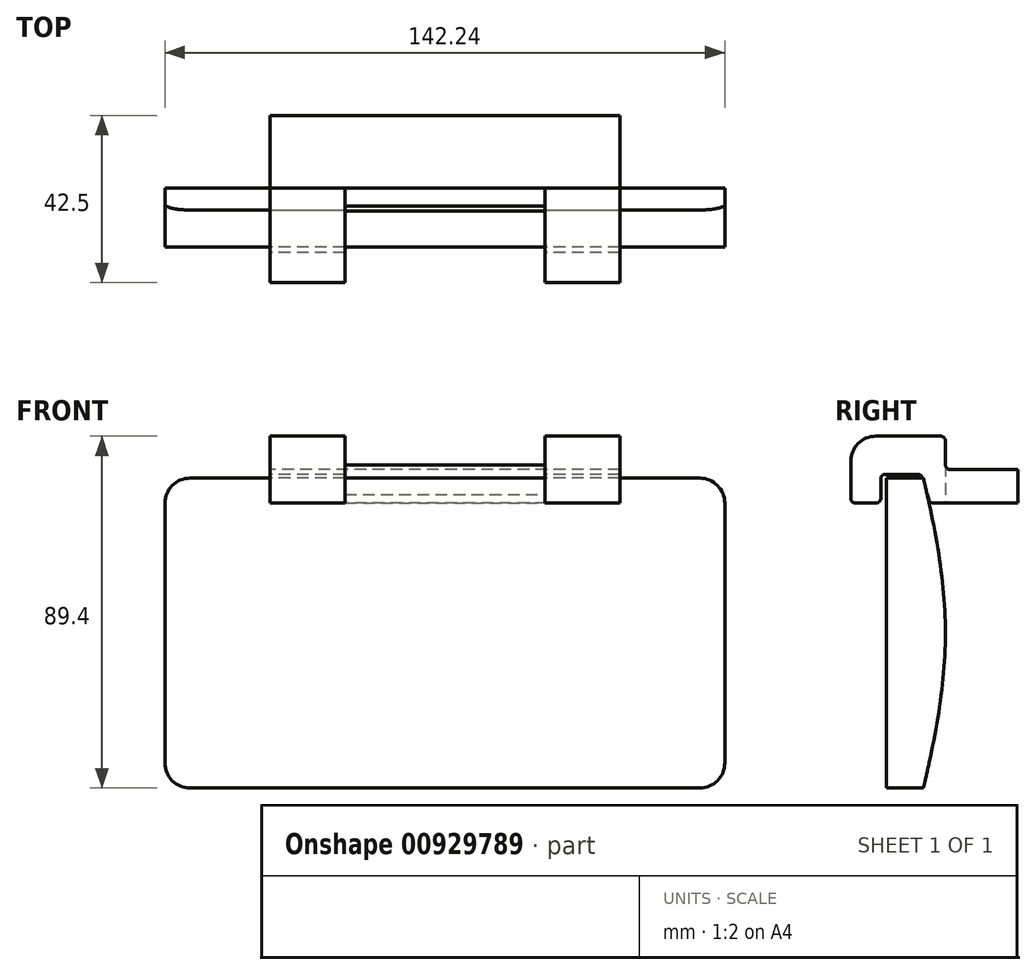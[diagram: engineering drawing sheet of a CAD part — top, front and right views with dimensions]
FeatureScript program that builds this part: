
annotation { "Feature Type Name" : "Feature", "Feature Type Description" : "" }
export const myFeature = defineFeature(function(context is Context, id is Id, definition is map)
    precondition{}
    {
        {
            var Q0;
            Q0=qCreatedBy(makeId("Front.planeOp"),FACE);
            var sketch = newSketch(context, id + "F0", { "sketchPlane" : qUnion([Q0])});
            skLineSegment(sketch, "E0.bottom", {"start": v(64.77, -39.37) * mm, "end": v(-64.77, -39.37) * mm});
            skLineSegment(sketch, "E0.top", {"start": v(64.77, 39.37) * mm, "end": v(-64.77, 39.37) * mm});
            skLineSegment(sketch, "E0.left", {"start": v(71.12, -33.02) * mm, "end": v(71.12, 33.02) * mm});
            skLineSegment(sketch, "E0.right", {"start": v(-71.12, -33.02) * mm, "end": v(-71.12, 33.02) * mm});
            skPoint(sketch, "E0.middle", {"position": v(0, 0) * mm});
            skLineSegment(sketch, "E1.0", {"start": v(71.12, 34.16) * mm, "end": v(-71.12, 34.16) * mm, "construction": true});
            skLineSegment(sketch, "E2.0", {"start": v(-65.91, -38.86) * mm, "end": v(-65.91, 39.37) * mm, "construction": true});
            skLineSegment(sketch, "E3.0", {"start": v(71.12, -34.16) * mm, "end": v(-71.12, -34.16) * mm, "construction": true});
            skLineSegment(sketch, "E4.0", {"start": v(65.91, -38.86) * mm, "end": v(65.91, 39.37) * mm, "construction": true});
            skPoint(sketch, "E5.visualSharp", {"position": v(71.12, 39.37) * mm});
            skArc(sketch, "E5.filletArc", {"start": v(71.12, 33.02) * mm, "mid": v(69.26, 37.51) * mm, "end": v(64.77, 39.37) * mm});
            skPoint(sketch, "E6.visualSharp", {"position": v(71.12, -39.37) * mm});
            skArc(sketch, "E6.filletArc", {"start": v(64.77, -39.37) * mm, "mid": v(69.26, -37.51) * mm, "end": v(71.12, -33.02) * mm});
            skPoint(sketch, "E7.visualSharp", {"position": v(-71.12, -39.37) * mm});
            skArc(sketch, "E7.filletArc", {"start": v(-71.12, -33.02) * mm, "mid": v(-69.26, -37.51) * mm, "end": v(-64.77, -39.37) * mm});
            skPoint(sketch, "E8.visualSharp", {"position": v(-71.12, 39.37) * mm});
            skArc(sketch, "E8.filletArc", {"start": v(-64.77, 39.37) * mm, "mid": v(-69.26, 37.51) * mm, "end": v(-71.12, 33.02) * mm});
            skSolve(sketch);
        }
        {
            var Q0;
            Q0=qSketchRegion(id+"F0",true);
            extrude(context, id + "F1", {"entities" : qUnion([Q0]), "depth" : 15 * mm});
        }
        {
            var Q0;
            Q0=makeQuery(id+"F1.opExtrude","SWEPT_FACE",FACE,{"disambiguationData":[OSD([sQuery(id+"F0.wireOp",EDGE,"E0.left")])]});
            var sketch = newSketch(context, id + "F2", { "sketchPlane" : qUnion([Q0])});
            skLineSegment(sketch, "E9", {"start": v(-14.99, 39.37) * mm, "end": v(-5.59, 39.37) * mm});
            skLineSegment(sketch, "E10", {"start": v(-14.99, 39.37) * mm, "end": v(-14.99, -39.37) * mm});
            skLineSegment(sketch, "E11", {"start": v(-5.59, 39.37) * mm, "end": v(-5.59, -39.37) * mm, "construction": true});
            skLineSegment(sketch, "E12", {"start": v(-14.99, -39.37) * mm, "end": v(-5.59, -39.37) * mm});
            skFitSpline(sketch, "E13", {"points": [v(-5.59, 39.37) * mm, v(0, 0) * mm, v(-5.59, -39.37) * mm], "startDerivative": vector(18.29, -78.23) * mm, "endDerivative": vector(-18.29, -78.23) * mm});
            skLineSegment(sketch, "E14.bottom", {"start": v(-5.59, 39.37) * mm, "end": v(0, 39.37) * mm});
            skLineSegment(sketch, "E14.left", {"start": v(-5.59, 39.37) * mm, "end": v(-5.59, -39.12) * mm});
            skLineSegment(sketch, "E14.right", {"start": v(0, 39.37) * mm, "end": v(0, -39.12) * mm});
            skLineSegment(sketch, "E15", {"start": v(-5.59, -39.37) * mm, "end": v(0, -39.37) * mm});
            skLineSegment(sketch, "E16", {"start": v(0, -39.37) * mm, "end": v(0, -39.12) * mm});
            skLineSegment(sketch, "E17", {"start": v(-5.59, -39.12) * mm, "end": v(-5.59, -39.37) * mm});
            skSolve(sketch);
        }
        {
            var Q0;
            {var subQ0=sQuery(id+"F2.wireOp",EDGE,"E14.bottom");Q0=makeQuery(id+"F2.imprint","IMPRINT",FACE,{"disambiguationData":[TD([[makeQuery(id+"F2.imprint","IMPRINT",EDGE,{"derivedFrom":subQ0}),-1.0]])]});}
            var Q1;
            {var subQ0=sQuery(id+"F2.wireOp",EDGE,"E14.right");var subQ1=sQuery(id+"F2.wireOp",EDGE,"E13");var subQ2=makeQuery(id+"F2.imprint","INTERSECT",VERTEX,{"derivedFrom":[subQ1,subQ0]});Q1=makeQuery(id+"F2.imprint","IMPRINT",FACE,{"disambiguationData":[TD([[makeQuery(id+"F2.imprint","IMPRINT",EDGE,{"disambiguationData":[TD([[subQ2,1.0]])],"derivedFrom":subQ1}),1.0]])]});}
            var Q2;
            {var subQ0=sQuery(id+"F2.wireOp",EDGE,"E14.right");var subQ1=sQuery(id+"F2.wireOp",EDGE,"E13");var subQ2=makeQuery(id+"F2.imprint","INTERSECT",VERTEX,{"derivedFrom":[subQ1,subQ0]});Q2=makeQuery(id+"F2.imprint","IMPRINT",FACE,{"disambiguationData":[TD([[makeQuery(id+"F2.imprint","IMPRINT",EDGE,{"disambiguationData":[TD([[subQ2,-1.0]])],"derivedFrom":subQ1}),1.0]])]});}
            var Q3;
            {var subQ0=sQuery(id+"F2.wireOp",EDGE,"E14.top");var subQ5=sQuery(id+"F2.wireOp",EDGE,"E14.right");var subQ6=makeQuery(id+"F2.imprint","INTERSECT",VERTEX,{"derivedFrom":[subQ0,subQ5]});Q3=makeQuery(id+"F2.imprint","IMPRINT",FACE,{"disambiguationData":[TD([[makeQuery(id+"F2.imprint","IMPRINT",EDGE,{"disambiguationData":[TD([[subQ6,1.0]])],"derivedFrom":subQ0}),1.0]])]});}
            var Q4;
            {var subQ0=sQuery(id+"F2.wireOp",EDGE,"E15");Q4=makeQuery(id+"F2.imprint","IMPRINT",FACE,{"disambiguationData":[TD([[makeQuery(id+"F2.imprint","IMPRINT",EDGE,{"derivedFrom":subQ0}),1.0]])]});}
            extrude(context, id + "F3", {"entities" : qUnion([Q0, Q1, Q2, Q3, Q4]), "operationType" : NewBodyOperationType.REMOVE, "endBound" : BoundingType.THROUGH_ALL, "oppositeDirection" : true, "depth" : 25.4 * mm, "offsetDistance" : 25.4 * mm});
        }
        {
            var Q0;
            Q0=qCreatedBy(makeId("Right.planeOp"),FACE);
            var sketch = newSketch(context, id + "F4", { "sketchPlane" : qUnion([Q0])});
            skLineSegment(sketch, "E18.bottom", {"start": v(-17.7, 50.03) * mm, "end": v(-1.22, 50.03) * mm});
            skLineSegment(sketch, "E18.top", {"start": v(-22.84, 33.04) * mm, "end": v(-17.62, 33.04) * mm});
            skLineSegment(sketch, "E18.left", {"start": v(-24.06, 43.68) * mm, "end": v(-24.06, 34.25) * mm});
            skLineSegment(sketch, "E18.right", {"start": v(18.44, 41.54) * mm, "end": v(18.44, 33.04) * mm});
            skPoint(sketch, "E19.visualSharp", {"position": v(-24.06, 50.03) * mm});
            skArc(sketch, "E19.filletArc", {"start": v(-17.7, 50.03) * mm, "mid": v(-22.2, 48.18) * mm, "end": v(-24.06, 43.68) * mm});
            skLineSegment(sketch, "E20.top", {"start": v(-15.4, 40.33) * mm, "end": v(-7.02, 40.33) * mm});
            skLineSegment(sketch, "E20.left", {"start": v(-16.4, 34.25) * mm, "end": v(-16.4, 39.3) * mm});
            skLineSegment(sketch, "E21", {"start": v(-5.85, 39.45) * mm, "end": v(-4.26, 33.92) * mm});
            skPoint(sketch, "E22.visualSharp", {"position": v(-16.4, 40.33) * mm});
            skArc(sketch, "E22.filletArc", {"start": v(-15.4, 40.33) * mm, "mid": v(-16.11, 40.03) * mm, "end": v(-16.4, 39.3) * mm});
            skLineSegment(sketch, "E23.trimOffspring", {"start": v(-3.1, 33.04) * mm, "end": v(18.44, 33.04) * mm});
            skLineSegment(sketch, "E24", {"start": v(18.44, 41.54) * mm, "end": v(1.22, 41.54) * mm});
            skLineSegment(sketch, "E25", {"start": v(0, 42.75) * mm, "end": v(0, 48.82) * mm});
            skPoint(sketch, "E26.orphan", {"position": v(18.44, 50.03) * mm});
            skLineSegment(sketch, "E27", {"start": v(0, 41.54) * mm, "end": v(0, 33.04) * mm});
            skPoint(sketch, "E28.visualSharp", {"position": v(0, 41.54) * mm});
            skArc(sketch, "E28.filletArc", {"start": v(0, 42.75) * mm, "mid": v(0.36, 41.9) * mm, "end": v(1.22, 41.54) * mm});
            skLineSegment(sketch, "E29", {"start": v(0, 41.54) * mm, "end": v(0, 44.9) * mm});
            skLineSegment(sketch, "E30", {"start": v(1.22, 41.54) * mm, "end": v(0, 41.54) * mm});
            skPoint(sketch, "E31.visualSharp", {"position": v(0, 50.03) * mm});
            skArc(sketch, "E31.filletArc", {"start": v(0, 48.82) * mm, "mid": v(-0.36, 49.68) * mm, "end": v(-1.22, 50.03) * mm});
            skPoint(sketch, "E32.visualSharp", {"position": v(-16.4, 33.04) * mm});
            skArc(sketch, "E32.filletArc", {"start": v(-17.62, 33.04) * mm, "mid": v(-16.76, 33.4) * mm, "end": v(-16.4, 34.25) * mm});
            skPoint(sketch, "E33.visualSharp", {"position": v(-4, 33.04) * mm});
            skArc(sketch, "E33.filletArc", {"start": v(-4.26, 33.92) * mm, "mid": v(-3.82, 33.28) * mm, "end": v(-3.1, 33.04) * mm});
            skPoint(sketch, "E34.visualSharp", {"position": v(-6.1, 40.33) * mm});
            skArc(sketch, "E34.filletArc", {"start": v(-5.85, 39.45) * mm, "mid": v(-6.3, 40.08) * mm, "end": v(-7.02, 40.33) * mm});
            skPoint(sketch, "E35.visualSharp", {"position": v(-24.06, 33.04) * mm});
            skArc(sketch, "E35.filletArc", {"start": v(-24.06, 34.25) * mm, "mid": v(-23.7, 33.4) * mm, "end": v(-22.84, 33.04) * mm});
            skSolve(sketch);
        }
        {
            var Q0;
            Q0 = qSketchRegion(id + "F4", true);
            extrude(context, id + "F5", {"entities" : qUnion([Q0]), "depth" : 44.45 * mm, "offsetDistance" : 25.4 * mm, "hasSecondDirection" : true, "secondDirectionOppositeDirection" : true, "secondDirectionDepth" : 44.45 * mm});
        }
        {
            var Q0;
            Q0=makeQuery(id+"F4.imprint","IMPRINT",FACE,{"disambiguationData":[TD([[makeQuery(id+"F4.imprint","IMPRINT",EDGE,{"derivedFrom":sQuery(id+"F4.wireOp",EDGE,"E18.bottom")}),-1.0]])]});
            extrude(context, id + "F6", {"entities" : qUnion([Q0]), "operationType" : NewBodyOperationType.REMOVE, "oppositeDirection" : true, "depth" : 25.4 * mm, "offsetDistance" : 25.4 * mm, "hasSecondDirection" : true, "secondDirectionOppositeDirection" : false, "secondDirectionDepth" : 25.4 * mm});
        }
    });
